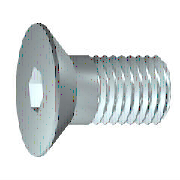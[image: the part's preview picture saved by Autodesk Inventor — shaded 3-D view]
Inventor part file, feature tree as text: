
AUTODESK INVENTOR PART (.ipt)
format: ipt  version: 2020 (Build 240168000, 168)  size: 190,464 bytes
history: native  units: mm (DEFAULTED — no unit token found)
features: other x5, sketch x2
ambient origin geometry x8: Origin, YZ Plane, XZ Plane, XY Plane, X Axis, Y Axis, Z Axis, Center Point
bodies: Solid1 (feature_tree)
feature tree (7):
  other  "WorkPoint1"
  sketch  "Skizze2"  dims[d0=45.0deg]
  other  "Drehung1"
  other  "MSC_A1"
  other  "MSC_PF1"
  other  "MSC_PT1"
  sketch  "Skizze3"  dims[d2=3.0mm d3=4.0mm d4=1.5mm d5=2.0mm d6=8.0mm d7=16.0mm d8=360.0deg d9=0.0mm d10=2.0mm d11=2.5mm d12=120.0deg d13=120.0deg d14=120.0deg d15=120.0deg d16=1.8mm d17=0.0mm d18=0.2mm d19=0.35mm d20=45.0deg d22=0.0mm d23=0.0mm d35=0.0mm d37=0.0mm d38=0.0mm d39=0.35mm d40=0.0mm d41=0.0mm d42=0.0mm d43=45.0deg]
